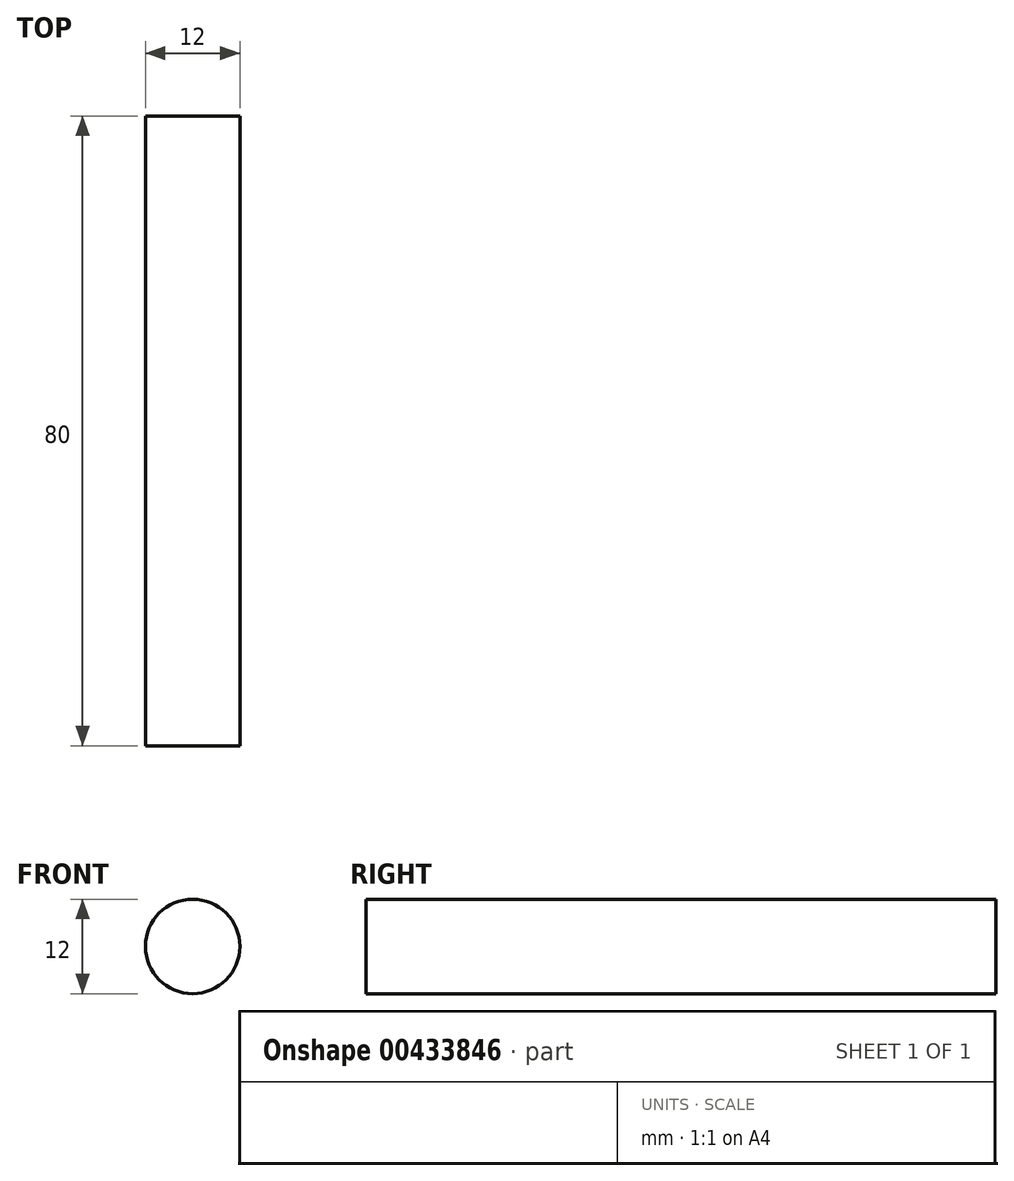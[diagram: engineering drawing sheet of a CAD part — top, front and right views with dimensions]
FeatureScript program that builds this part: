
annotation { "Feature Type Name" : "Feature", "Feature Type Description" : "" }
export const myFeature = defineFeature(function(context is Context, id is Id, definition is map)
    precondition{}
    {
        {
            var Q0;
            Q0=qCreatedBy(makeId("Front.planeOp"),FACE);
            var sketch = newSketch(context, id + "F0", { "sketchPlane" : qUnion([Q0])});
            skCircle(sketch, "E0", {"center": v(0, 0) * mm, "radius": 6 * mm});
            skSolve(sketch);
        }
        {
            var Q0;
            Q0 = qSketchRegion(id + "F0", true);
            extrude(context, id + "F1", {"entities" : qUnion([Q0]), "depth" : 80 * mm});
        }
    });
